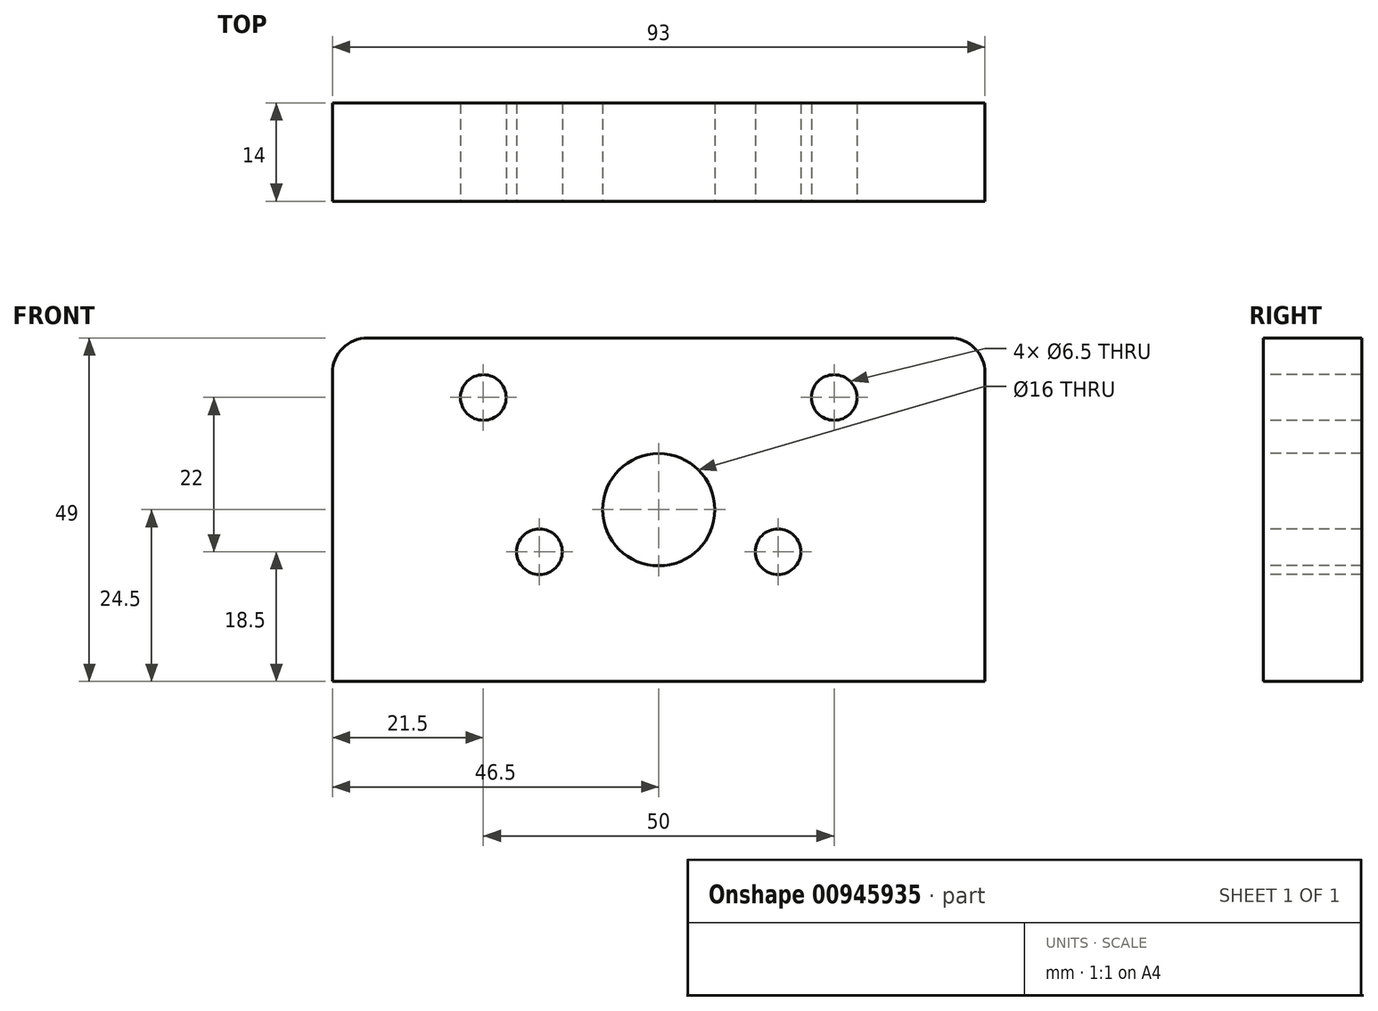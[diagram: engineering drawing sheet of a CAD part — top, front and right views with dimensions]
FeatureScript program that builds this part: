
annotation { "Feature Type Name" : "Feature", "Feature Type Description" : "" }
export const myFeature = defineFeature(function(context is Context, id is Id, definition is map)
    precondition{}
    {
        {
            var Q0;
            Q0=qCreatedBy(makeId("Front.planeOp"),FACE);
            var sketch = newSketch(context, id + "F0", { "sketchPlane" : qUnion([Q0])});
            skLineSegment(sketch, "E0.bottom", {"start": v(46.5, -24.5) * mm, "end": v(-46.5, -24.5) * mm});
            skLineSegment(sketch, "E0.top", {"start": v(41.5, 24.5) * mm, "end": v(-41.5, 24.5) * mm});
            skLineSegment(sketch, "E0.left", {"start": v(46.5, -24.5) * mm, "end": v(46.5, 19.5) * mm});
            skLineSegment(sketch, "E0.right", {"start": v(-46.5, -24.5) * mm, "end": v(-46.5, 19.5) * mm});
            skPoint(sketch, "E0.middle", {"position": v(0, 0) * mm});
            skPoint(sketch, "E1.visualSharp", {"position": v(-46.5, 24.5) * mm});
            skArc(sketch, "E1.filletArc", {"start": v(-41.5, 24.5) * mm, "mid": v(-45.04, 23.04) * mm, "end": v(-46.5, 19.5) * mm});
            skPoint(sketch, "E2.visualSharp", {"position": v(46.5, 24.5) * mm});
            skArc(sketch, "E2.filletArc", {"start": v(46.5, 19.5) * mm, "mid": v(45.04, 23.04) * mm, "end": v(41.5, 24.5) * mm});
            skSolve(sketch);
        }
        {
            var Q0;
            Q0 = qSketchRegion(id + "F0", true);
            extrude(context, id + "F1", {"entities" : qUnion([Q0]), "depth" : 14 * mm, "offsetDistance" : 25 * mm});
        }
        {
            var Q0;
            Q0=makeQuery(id+"F1.opExtrude","CAP_FACE",FACE,{"disambiguationData":[OSD([sQuery(id+"F0.wireOp",EDGE,"E0.bottom"),sQuery(id+"F0.wireOp",EDGE,"E0.top"),sQuery(id+"F0.wireOp",EDGE,"E0.left"),sQuery(id+"F0.wireOp",EDGE,"E0.right"),sQuery(id+"F0.wireOp",EDGE,"E1.filletArc"),sQuery(id+"F0.wireOp",EDGE,"E2.filletArc")])],"isStart":false});
            var sketch = newSketch(context, id + "F2", { "sketchPlane" : qUnion([Q0])});
            skCircle(sketch, "E3", {"center": v(0, 0) * mm, "radius": 8 * mm});
            skCircle(sketch, "E4", {"center": v(-17, -6) * mm, "radius": 3.25 * mm});
            skCircle(sketch, "E5", {"center": v(-25, 16) * mm, "radius": 3.25 * mm});
            skLineSegment(sketch, "E6", {"start": v(0, 24.5) * mm, "end": v(0, -24.5) * mm, "construction": true});
            skCircle(sketch, "E7.MirrorC", {"center": v(25, 16) * mm, "radius": 3.25 * mm});
            skCircle(sketch, "E8.MirrorC", {"center": v(17, -6) * mm, "radius": 3.25 * mm});
            skSolve(sketch);
        }
        {
            var Q0;
            Q0 = qSketchRegion(id + "F2", true);
            extrude(context, id + "F3", {"entities" : qUnion([Q0]), "operationType" : NewBodyOperationType.REMOVE, "endBound" : BoundingType.THROUGH_ALL, "oppositeDirection" : true, "depth" : 25 * mm, "offsetDistance" : 25 * mm});
        }
    });
